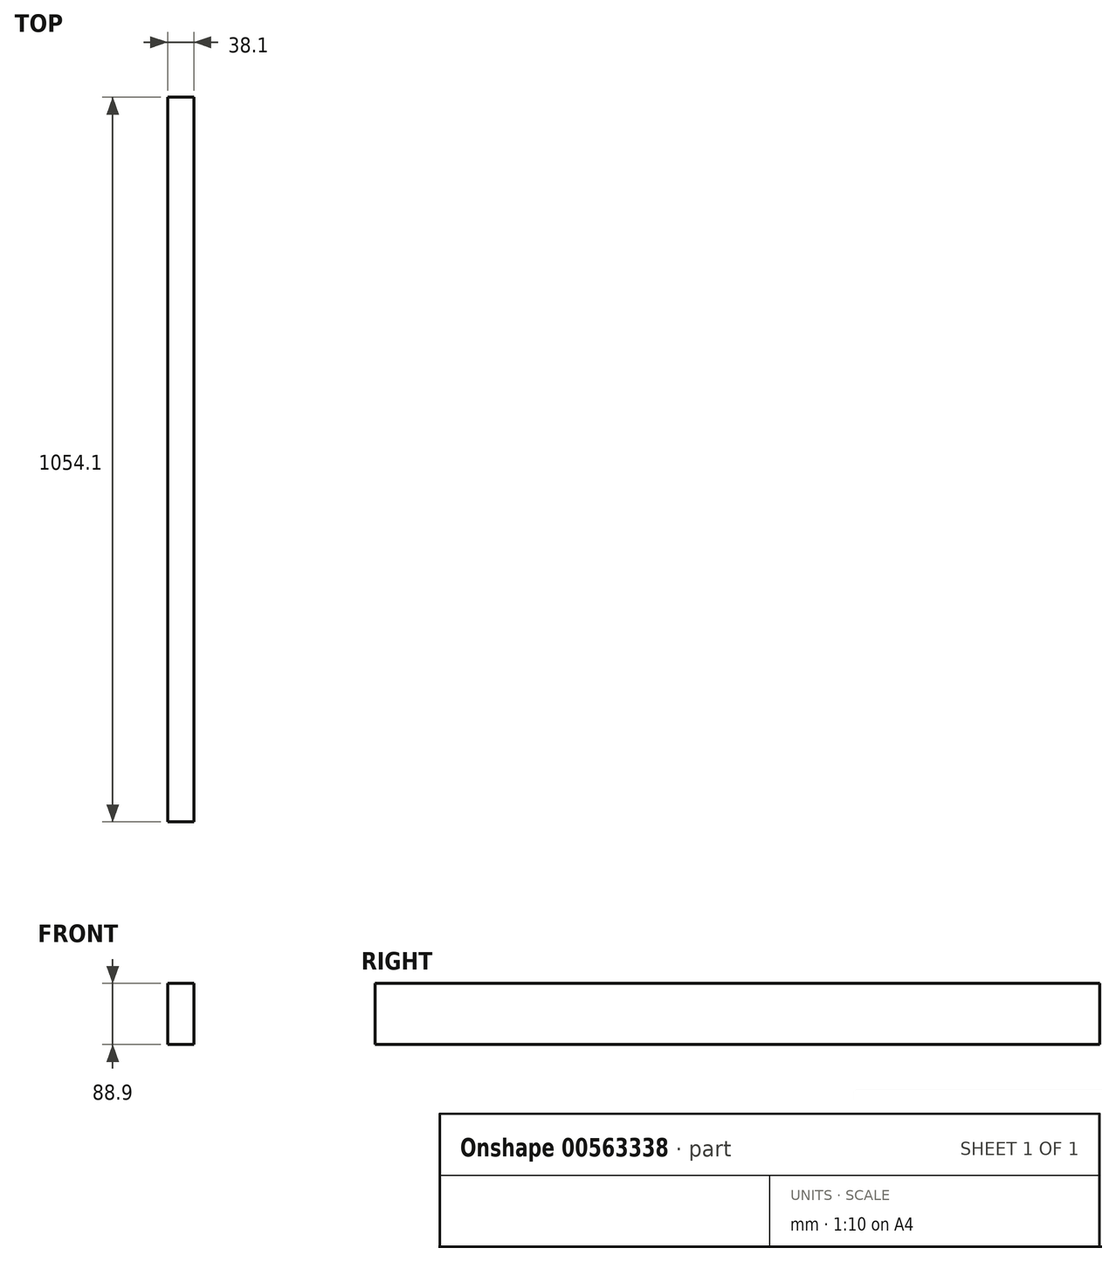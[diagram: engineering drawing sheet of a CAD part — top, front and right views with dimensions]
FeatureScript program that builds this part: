
annotation { "Feature Type Name" : "Feature", "Feature Type Description" : "" }
export const myFeature = defineFeature(function(context is Context, id is Id, definition is map)
    precondition{}
    {
        {
            var Q0;
            Q0=qCreatedBy(makeId("Top.planeOp"),FACE);
            var sketch = newSketch(context, id + "F0", { "sketchPlane" : qUnion([Q0])});
            skLineSegment(sketch, "E0.bottom", {"start": v(-19.05, -527.05) * mm, "end": v(19.05, -527.05) * mm});
            skLineSegment(sketch, "E0.top", {"start": v(-19.05, 527.05) * mm, "end": v(19.05, 527.05) * mm});
            skLineSegment(sketch, "E0.left", {"start": v(-19.05, -527.05) * mm, "end": v(-19.05, 527.05) * mm});
            skLineSegment(sketch, "E0.right", {"start": v(19.05, -527.05) * mm, "end": v(19.05, 527.05) * mm});
            skPoint(sketch, "E0.middle", {"position": v(0, 0) * mm});
            skSolve(sketch);
        }
        {
            var Q0;
            Q0 = qSketchRegion(id + "F0", true);
            extrude(context, id + "F1", {"entities" : qUnion([Q0]), "depth" : 88.9 * mm, "offsetDistance" : 25.4 * mm});
        }
    });
